# Revit family: Toilet_Universal-Floor_Mount-Sloan-ST-2229_Series
name_source: partatom
category: Plumbing Fixtures
revit_build: Autodesk Revit 2014 (Build: 20130308_1515(x64)
units: mm (PartAtom-declared; Revit-internal decimal feet)

## types (2) — shared parameters
ADA Compliant = Yes
Assembly Code = D2010110
CW Connection = Yes
Default Elevation = 0"
Fixture Color = White
Flush Volume = 1.1 to 1.6 gpf / 4.2 to 6.0 Lpf
HW Connection = No
HWFU = 10
High Efficiency = Yes
Manufacturer = Sloan
Material = Vitreous China-Sloan-White
Mounting = Floor Mount
Price = Prices may vary. Please consult Sloan Rep for most up-to-date price list.
Product Documentation Link = https://specifications.sloan.com
Product Page URL = https://www.sloan.com
Spud Inlet Size = 1-1/2" I.P.S
Spud Location = Top Spud
URL = http://www.sloan.com
Vent Connection = Yes
WFU = 10
Waste Connection = Yes

## per-type parameters (varying)
| type | Description | Order Code |
| ST-2229-STG | Complete ADA compliant vitreous china water closet with SloanTec hydrophobic antimicrobial glaze. | 2172229 |
| ST-2229 | Complete ADA compliant vitreous china water closet. | 2102229 |

note: column(s) folded — value = type name in every type: Model

## geometry (parser evidence)
native form markers: Sweep x1
no freeform markers — native parametric forms only
